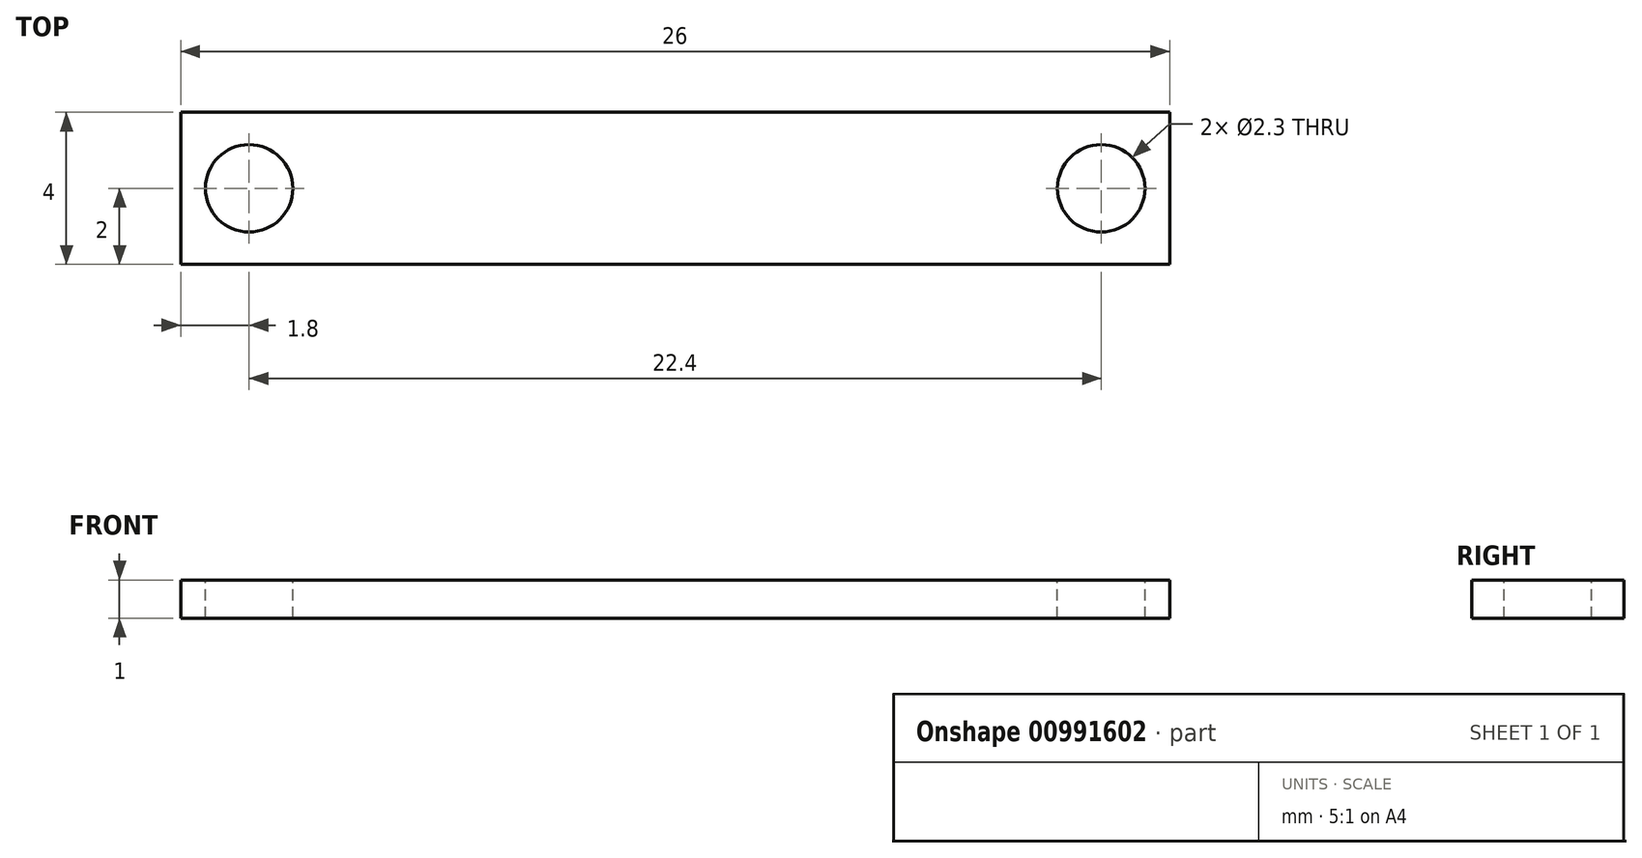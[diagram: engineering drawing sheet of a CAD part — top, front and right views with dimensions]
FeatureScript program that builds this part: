
annotation { "Feature Type Name" : "Feature", "Feature Type Description" : "" }
export const myFeature = defineFeature(function(context is Context, id is Id, definition is map)
    precondition{}
    {
        {
            var Q0;
            Q0=qCreatedBy(makeId("Top.planeOp"),FACE);
            var sketch = newSketch(context, id + "F0", { "sketchPlane" : qUnion([Q0])});
            skLineSegment(sketch, "E0.top", {"start": v(-13, -2) * mm, "end": v(13, -2) * mm});
            skLineSegment(sketch, "E0.left", {"start": v(-13, 2) * mm, "end": v(-13, -2) * mm});
            skLineSegment(sketch, "E0.right", {"start": v(13, 2) * mm, "end": v(13, -2) * mm});
            skLineSegment(sketch, "E1", {"start": v(-8.08, 0) * mm, "end": v(8.08, 0) * mm, "construction": true});
            skLineSegment(sketch, "E2", {"start": v(0, 4.1) * mm, "end": v(0, -4.67) * mm, "construction": true});
            skLineSegment(sketch, "E3", {"start": v(-13, 2) * mm, "end": v(13, 2) * mm});
            skSolve(sketch);
        }
        {
            var Q0;
            Q0=qSketchRegion(id+"F0",true);
            extrude(context, id + "F1", {"entities" : qUnion([Q0]), "depth" : 1 * mm, "offsetDistance" : 25 * mm});
        }
        {
            var Q0;
            Q0=makeQuery(id+"F1.opExtrude","CAP_FACE",FACE,{"disambiguationData":[OSD([sQuery(id+"F0.wireOp",EDGE,"E0.top"),sQuery(id+"F0.wireOp",EDGE,"E0.left"),sQuery(id+"F0.wireOp",EDGE,"E0.right"),sQuery(id+"F0.wireOp",EDGE,"E3")])],"isStart":false});
            var sketch = newSketch(context, id + "F2", { "sketchPlane" : qUnion([Q0])});
            skPoint(sketch, "E4", {"position": v(-11.2, 0) * mm});
            skPoint(sketch, "E5", {"position": v(11.2, 0) * mm});
            skLineSegment(sketch, "E6", {"start": v(-5.62, 0) * mm, "end": v(5.7, 0) * mm, "construction": true});
            skPoint(sketch, "E6.endSnap0", {"position": v(13, 0) * mm});
            skLineSegment(sketch, "E7", {"start": v(0, 2.43) * mm, "end": v(0, -2.95) * mm, "construction": true});
            skSolve(sketch);
        }
        {
            var Q0;
            Q0=sQuery(id+"F2.wireOp",VERTEX,"E4");
            var Q1;
            Q1=sQuery(id+"F2.wireOp",VERTEX,"E5");
            var Q2;
            Q2=makeQuery(id+"F1.opExtrude","SWEPT_BODY",BODY,{"disambiguationData":[OSD([sQuery(id+"F0.wireOp",EDGE,"E0.top"),sQuery(id+"F0.wireOp",EDGE,"E0.left"),sQuery(id+"F0.wireOp",EDGE,"E0.right"),sQuery(id+"F0.wireOp",EDGE,"E3")])]});
            hole(context, id + "F3", {"style" : HoleStyle.SIMPLE, "endStyle" : HoleEndStyle.THROUGH, "holeDiameter" : 2.3 * mm, "majorDiameter" : 5 * mm, "isTappedThrough" : true, "tappedDepth" : 12 * mm, "tapClearance" : 3, "locations" : qUnion([Q0, Q1]), "scope" : qUnion([Q2])});
        }
    });
